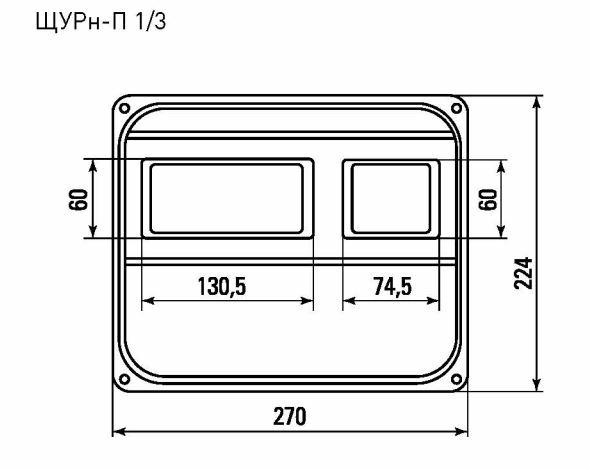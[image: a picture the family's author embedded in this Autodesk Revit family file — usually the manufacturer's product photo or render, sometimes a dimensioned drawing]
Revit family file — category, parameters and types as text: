
# Revit family: EKF_EE_ЩМПг_IP54_PROxima
name_source: partatom
category: Электрооборудование
units: mm (PartAtom-declared; Revit-internal decimal feet)

## family parameters
Всегда вертикально = Да
На основе рабочей плоскости = Нет
Общий = Нет
При загрузке вырезать с полостями = Нет
Размер круглого соединителя = Использовать диаметр
Тип детали = Силовой щит
Точка расчета площади = Да

## types (14) — shared parameters
ADSK_Единица измерения = компл.
ADSK_Завод-изготовитель = EKF
ADSK_Классификация нагрузок = Прочее
ADSK_Количество = 1
ADSK_Количество фаз = 3
ADSK_Коэффициент мощности = 1
ADSK_Материал = RAL 7035_Сталь
ADSK_Напряжение = 400 В
ADSK_Номинальная мощность = 0 Вт
ADSK_Полная мощность = 0 В·А
ADSK_Ток = 125 А
Изготовитель = EKF
Серия номенклатуры = Basic
Степень защиты IP = IP54
ТВ = EKF
Тип установки = Навесной
zero-valued in all types: Количество DIN-реек, Количество модулей на DIN-рейке, Максимальное количество модулей

## per-type parameters (varying)
| type | ADSK_Код изделия | ADSK_Марка | ADSK_Масса | ADSK_Наименование | ADSK_Обозначение | ADSK_Размер_Высота | ADSK_Размер_Глубина | ADSK_Размер_Ширина | Описание | Тип |
| ЩМПг-100.65.30 (ЩРНМ-5) IP54 PROxima | mb24-5 | ЩМПг-100.65.30 (ЩРНМ-5) IP54 | 33.03 | Щит с монтажной панелью ЩМПг-100.65.30 (ЩРНМ-5) IP54 PROxima | ЩМПг-100.65.30 (ЩРНМ-5) IP54 | 1000 мм | 300 мм | 650 мм | Щит с монтажной панелью ЩМПг-100.65.30 (ЩРНМ-5) IP54 PROxima | 99 мм |
| ЩМПг-120.75.30 (ЩРНМ-6) IP54 PROxima | mb24-6 | ЩМПг-120.75.30 (ЩРНМ-6) IP54 | 42.78 | Щит с монтажной панелью ЩМПг-120.75.30 (ЩРНМ-6) IP54 PROxima | ЩМПг-120.75.30 (ЩРНМ-6) IP54 | 1200 мм | 300 мм | 750 мм | Щит с монтажной панелью ЩМПг-120.75.30 (ЩРНМ-6) IP54 PROxima | 100 мм |
| ЩМПг-132.75.30 (ЩРНМ-7) IP54 EKF PROxima | mb24-07 | ЩМПг-132.75.30 (ЩРНМ-7) IP54 | 40.2 | Щит с монтажной панелью ЩМПг-132.75.30 (ЩРНМ-7) IP54 EKF PROxima | ЩМПг-132.75.30 (ЩРНМ-7) IP54 | 1320 мм | 300 мм | 750 мм | Щит с монтажной панелью ЩМПг-132.75.30 (ЩРНМ-7) IP54 EKF PROxima | 101 мм |
| ЩМПг-80.60.25 (ЩРНМ-4) IP54 EKF PROxima | mb24-4 | ЩМПг- 80.60.25 (ЩРНМ-4) IP54 | 24.15 | Щит с монтажной панелью ЩМПг- 80.60.25 (ЩРНМ-4) IP54 EKF PROxima | ЩМПг- 80.60.25 (ЩРНМ-4) IP54 | 800 мм | 250 мм | 600 мм | Щит с монтажной панелью ЩМПг- 80.60.25 (ЩРНМ-4) IP54 EKF PROxima | 98 мм |
| ЩМПг-65.50.22 (ЩРНМ-3) IP54 EKF PROxima | mb24-3 | ЩМПг- 65.50.22 (ЩРНМ-3) IP54 | 15.76 | Щит с монтажной панелью ЩМПг- 65.50.22 (ЩРНМ-3) IP54 EKF PROxima | ЩМПг- 65.50.22 (ЩРНМ-3) IP54 | 650 мм | 220 мм | 500 мм | Щит с монтажной панелью ЩМПг- 65.50.22 (ЩРНМ-3) IP54 EKF PROxima | 97 мм |
| ЩМПг-60.60.25 IP54 EKF PROxima | mb24-06 | ЩМПг- 60.60.25 IP54 | 15 | Щит с монтажной панелью ЩМПг- 60.60.25 IP54 EKF PROxima | ЩМПг- 60.60.25 IP54 | 600 мм | 250 мм | 600 мм | Щит с монтажной панелью ЩМПг- 60.60.25 IP54 EKF PROxima | 96 мм |
| ЩМПг-50.40.22 (ЩРНМ-2) IP54 EKF PROxima | mb24-2 | ЩМПг- 50.40.22 (ЩРНМ-2) IP54 | 11.39 | Щит с монтажной панелью ЩМПг- 50.40.22 (ЩРНМ-2) IP54 EKF PROxima | ЩМПг- 50.40.22 (ЩРНМ-2) IP54 | 500 мм | 220 мм | 400 мм | Щит с монтажной панелью ЩМПг- 50.40.22 (ЩРНМ-2) IP54 EKF PROxima | 95 мм |
| ЩМПг-40.60.25 IP54 EKF PROxima | mb24-05 | ЩМПг- 40.60.25 IP54 | 11 | Щит с монтажной панелью ЩМПг- 40.60.25 IP54 EKF PROxima | ЩМПг- 40.60.25 IP54 | 400 мм | 250 мм | 600 мм | Щит с монтажной панелью ЩМПг- 40.60.25 IP54 EKF PROxima | 94 мм |
| ЩМПг-40.40.25 IP54 EKF PROxima | mb24-04 | ЩМПг- 40.40.25 IP54 | 7.8 | Щит с монтажной панелью ЩМПг- 40.40.25 IP54 EKF PROxima | ЩМПг- 40.40.25 IP54 | 400 мм | 250 мм | 400 мм | Щит с монтажной панелью ЩМПг- 40.40.25 IP54 EKF PROxima | 93 мм |
| ЩМПг-40.40.15 IP54 EKF PROxima | mb24-003 | ЩМПг- 40.40.15 IP54 | 6.5 | Щит с монтажной панелью ЩМПг- 40.40.15 IP54 EKF PROxima | ЩМПг- 40.40.15 IP54 | 400 мм | 150 мм | 400 мм | Щит с монтажной панелью ЩМПг- 40.40.15 IP54 EKF PROxima | 92 мм |
| ЩМПг-40.30.22 (ЩРНМ-1) IP54 EKF PROxima | mb24-1 | ЩМПг- 40.30.22 (ЩРНМ-1) IP54 | 7.2 | Щит с монтажной панелью ЩМПг- 40.30.22 (ЩРНМ-1) IP54 EKF PROxima | ЩМПг- 40.30.22 (ЩРНМ-1) IP54 | 400 мм | 220 мм | 300 мм | Щит с монтажной панелью ЩМПг- 40.30.22 (ЩРНМ-1) IP54 EKF PROxima | 91 мм |
| ЩМПг-40.21.15 IP54 EKF PROxima | mb24-22 | ЩМПг- 40.21.15 IP54 | 10.92 | Щит с монтажной панелью ЩМПг- 40.21.15 IP54 EKF PROxima | ЩМПг- 40.21.15 IP54 | 400 мм | 150 мм | 210 мм | Щит с монтажной панелью ЩМПг- 40.21.15 IP54 EKF PROxima | 90 мм |
| ЩМПг-30.21.15 IP54 EKF PROxima | mb24-02 | ЩМПг- 30.21.15 IP54 | 2.8 | Щит с монтажной панелью ЩМПг- 30.21.15 IP54 EKF PROxima | ЩМПг- 30.21.15 IP54 | 300 мм | 150 мм | 210 мм | Щит с монтажной панелью ЩМПг- 30.21.15 IP54 EKF PROxima | 89 мм |
| ЩМПг-25.30.15 IP54 EKF PROxima | mb24-01 | ЩМПг- 25.30.15 IP54 | 4.3 | Щит с монтажной панелью ЩМПг- 25.30.15 IP54 EKF PROxima | ЩМПг- 25.30.15 IP54 | 250 мм | 150 мм | 300 мм | Щит с монтажной панелью ЩМПг- 25.30.15 IP54 EKF PROxima | 88 мм |
